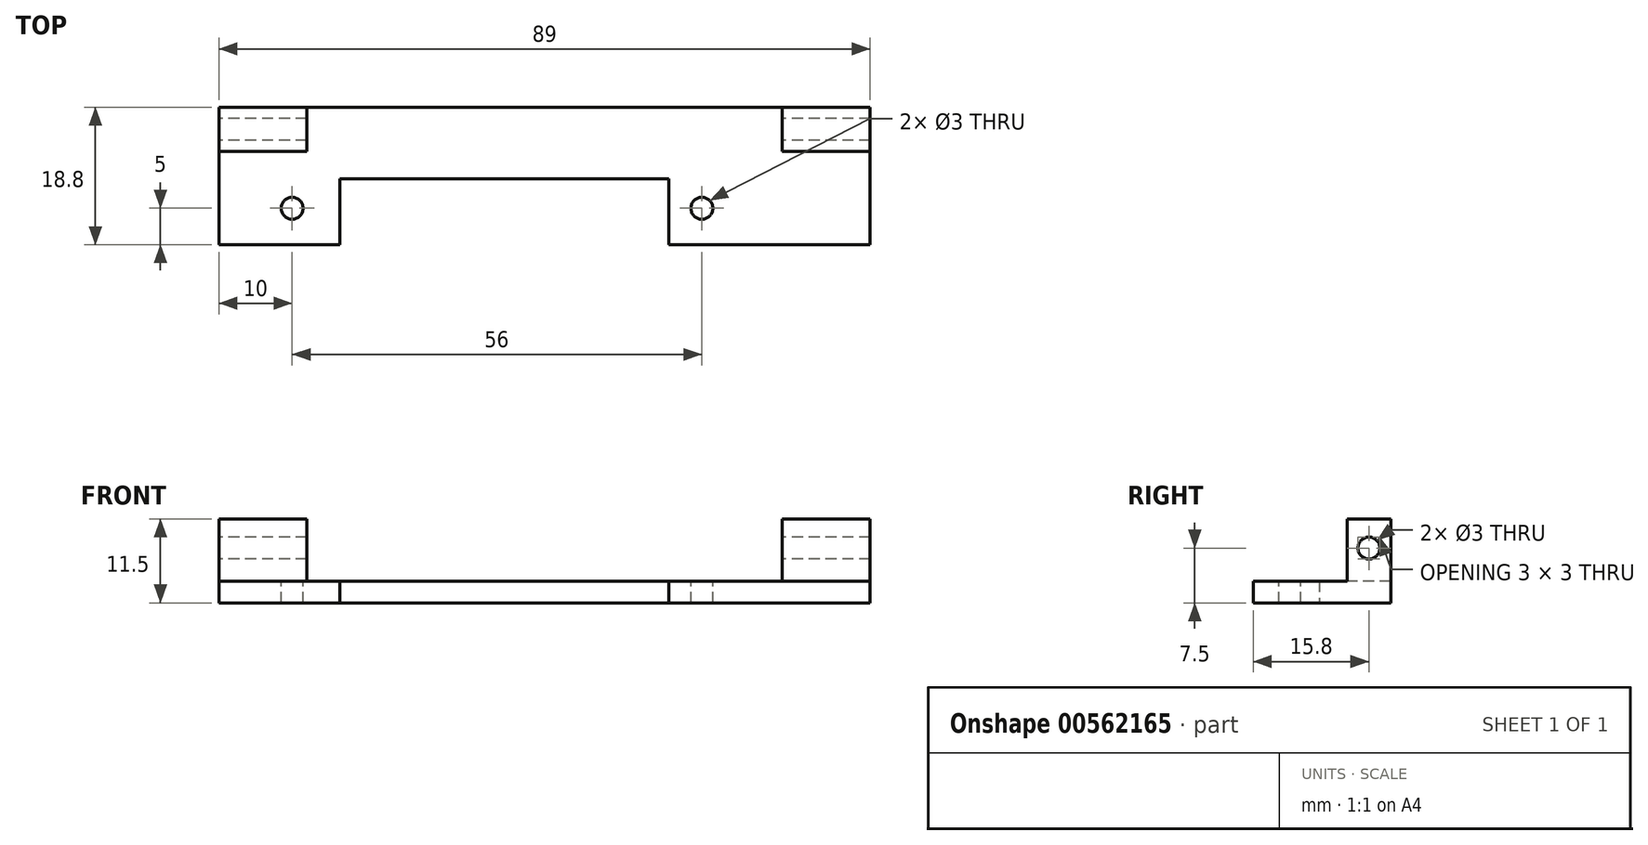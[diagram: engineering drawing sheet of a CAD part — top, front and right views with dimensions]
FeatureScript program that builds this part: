
annotation { "Feature Type Name" : "Feature", "Feature Type Description" : "" }
export const myFeature = defineFeature(function(context is Context, id is Id, definition is map)
    precondition{}
    {
        {
            var Q0;
            Q0=qCreatedBy(makeId("Top.planeOp"),FACE);
            var sketch = newSketch(context, id + "F0", { "sketchPlane" : qUnion([Q0])});
            skLineSegment(sketch, "E0.bottom", {"start": v(44.5, -9.4) * mm, "end": v(-44.5, -9.4) * mm});
            skLineSegment(sketch, "E0.top", {"start": v(44.5, 9.4) * mm, "end": v(-44.5, 9.4) * mm});
            skLineSegment(sketch, "E0.left", {"start": v(44.5, -9.4) * mm, "end": v(44.5, 9.4) * mm});
            skLineSegment(sketch, "E0.right", {"start": v(-44.5, -9.4) * mm, "end": v(-44.5, 9.4) * mm});
            skPoint(sketch, "E0.middle", {"position": v(0, 0) * mm});
            skSolve(sketch);
        }
        {
            var Q0;
            Q0=makeQuery(id+"F0.imprint","IMPRINT",FACE,{"disambiguationData":[TD([[makeQuery(id+"F0.imprint","IMPRINT",EDGE,{"derivedFrom":sQuery(id+"F0.wireOp",EDGE,"E0.bottom")}),-1.0]])]});
            extrude(context, id + "F1", {"entities" : qUnion([Q0]), "depth" : 3 * mm, "offsetDistance" : 25 * mm});
        }
        {
            var Q0;
            Q0=makeQuery(id+"F1.opExtrude","CAP_FACE",FACE,{"disambiguationData":[OSD([sQuery(id+"F0.wireOp",EDGE,"E0.bottom"),sQuery(id+"F0.wireOp",EDGE,"E0.top"),sQuery(id+"F0.wireOp",EDGE,"E0.left"),sQuery(id+"F0.wireOp",EDGE,"E0.right")])],"isStart":false});
            var sketch = newSketch(context, id + "F2", { "sketchPlane" : qUnion([Q0])});
            skLineSegment(sketch, "E1.bottom", {"start": v(44.5, 9.4) * mm, "end": v(32.5, 9.4) * mm});
            skLineSegment(sketch, "E1.top", {"start": v(44.5, 3.4) * mm, "end": v(32.5, 3.4) * mm});
            skLineSegment(sketch, "E1.left", {"start": v(44.5, 9.4) * mm, "end": v(44.5, 3.4) * mm});
            skLineSegment(sketch, "E1.right", {"start": v(32.5, 9.4) * mm, "end": v(32.5, 3.4) * mm});
            skSolve(sketch);
        }
        {
            var Q0;
            {var subQ4=sQuery(id+"F2.wireOp",EDGE,"E1.top");Q0=makeQuery(id+"F2.imprint","IMPRINT",FACE,{"disambiguationData":[TD([[makeQuery(id+"F2.imprint","IMPRINT",EDGE,{"derivedFrom":subQ4}),1.0]])]});}
            var sketch = newSketch(context, id + "F3", { "sketchPlane" : qUnion([Q0])});
            skLineSegment(sketch, "E2.bottom", {"start": v(-44.5, 9.4) * mm, "end": v(-32.5, 9.4) * mm});
            skLineSegment(sketch, "E2.top", {"start": v(-44.5, 3.4) * mm, "end": v(-32.5, 3.4) * mm});
            skLineSegment(sketch, "E2.left", {"start": v(-44.5, 9.4) * mm, "end": v(-44.5, 3.4) * mm});
            skLineSegment(sketch, "E2.right", {"start": v(-32.5, 9.4) * mm, "end": v(-32.5, 3.4) * mm});
            skSolve(sketch);
        }
        {
            var Q0;
            Q0=makeQuery(id+"F2.imprint","IMPRINT",FACE,{"disambiguationData":[TD([[makeQuery(id+"F2.imprint","IMPRINT",EDGE,{"derivedFrom":sQuery(id+"F2.wireOp",EDGE,"E1.bottom")}),1.0]])]});
            var Q1;
            Q1=makeQuery(id+"F3.imprint","IMPRINT",FACE,{"disambiguationData":[TD([[makeQuery(id+"F3.imprint","IMPRINT",EDGE,{"derivedFrom":sQuery(id+"F3.wireOp",EDGE,"E2.bottom")}),1.0]])]});
            extrude(context, id + "F4", {"entities" : qUnion([Q0, Q1]), "operationType" : NewBodyOperationType.ADD, "depth" : 8.5 * mm, "offsetDistance" : 25 * mm});
        }
        {
            var Q0;
            Q0=makeQuery(id+"F4.boolean.opBoolean","MERGE",FACE,{"derivedFrom":[makeQuery(id+"F1.opExtrude","SWEPT_FACE",FACE,{"disambiguationData":[OSD([sQuery(id+"F0.wireOp",EDGE,"E0.right")])]}),makeQuery(id+"F4.opExtrude","SWEPT_FACE",FACE,{"disambiguationData":[OSD([sQuery(id+"F3.wireOp",EDGE,"E2.left")])]})]});
            var sketch = newSketch(context, id + "F5", { "sketchPlane" : qUnion([Q0])});
            skCircle(sketch, "E3", {"center": v(-6.4, 7.5) * mm, "radius": 1.5 * mm});
            skSolve(sketch);
        }
        {
            var Q0;
            Q0=makeQuery(id+"F5.imprint","IMPRINT",FACE,{"disambiguationData":[TD([[makeQuery(id+"F5.imprint","IMPRINT",EDGE,{"derivedFrom":sQuery(id+"F5.wireOp",EDGE,"E3")}),1.0]])]});
            extrude(context, id + "F6", {"entities" : qUnion([Q0]), "operationType" : NewBodyOperationType.REMOVE, "endBound" : BoundingType.THROUGH_ALL, "oppositeDirection" : true, "depth" : 25 * mm, "offsetDistance" : 25 * mm});
        }
        {
            var Q0;
            Q0=makeQuery(id+"F1.opExtrude","CAP_FACE",FACE,{"disambiguationData":[OSD([sQuery(id+"F0.wireOp",EDGE,"E0.bottom"),sQuery(id+"F0.wireOp",EDGE,"E0.top"),sQuery(id+"F0.wireOp",EDGE,"E0.left"),sQuery(id+"F0.wireOp",EDGE,"E0.right")])],"isStart":false});
            var sketch = newSketch(context, id + "F7", { "sketchPlane" : qUnion([Q0])});
            skCircle(sketch, "E4", {"center": v(21.5, -4.4) * mm, "radius": 1.5 * mm});
            skSolve(sketch);
        }
        {
            var Q0;
            Q0=makeQuery(id+"F7.imprint","IMPRINT",FACE,{"disambiguationData":[TD([[makeQuery(id+"F7.imprint","IMPRINT",EDGE,{"derivedFrom":sQuery(id+"F7.wireOp",EDGE,"E4")}),-1.0]])]});
            var sketch = newSketch(context, id + "F8", { "sketchPlane" : qUnion([Q0])});
            skCircle(sketch, "E5", {"center": v(-34.5, -4.4) * mm, "radius": 1.5 * mm});
            skSolve(sketch);
        }
        {
            var Q0;
            Q0=makeQuery(id+"F7.imprint","IMPRINT",FACE,{"disambiguationData":[TD([[makeQuery(id+"F7.imprint","IMPRINT",EDGE,{"derivedFrom":sQuery(id+"F7.wireOp",EDGE,"E4")}),1.0]])]});
            var Q1;
            Q1=makeQuery(id+"F8.imprint","IMPRINT",FACE,{"disambiguationData":[TD([[makeQuery(id+"F8.imprint","IMPRINT",EDGE,{"derivedFrom":sQuery(id+"F8.wireOp",EDGE,"E5")}),1.0]])]});
            extrude(context, id + "F9", {"entities" : qUnion([Q0, Q1]), "operationType" : NewBodyOperationType.REMOVE, "oppositeDirection" : true, "depth" : 15 * mm, "offsetDistance" : 25 * mm});
        }
        {
            var Q0;
            Q0=makeQuery(id+"F1.opExtrude","CAP_FACE",FACE,{"disambiguationData":[OSD([sQuery(id+"F0.wireOp",EDGE,"E0.bottom"),sQuery(id+"F0.wireOp",EDGE,"E0.top"),sQuery(id+"F0.wireOp",EDGE,"E0.left"),sQuery(id+"F0.wireOp",EDGE,"E0.right")])],"isStart":true});
            var sketch = newSketch(context, id + "F10", { "sketchPlane" : qUnion([Q0])});
            skLineSegment(sketch, "E6.bottom", {"start": v(-28, 9.4) * mm, "end": v(17, 9.4) * mm});
            skLineSegment(sketch, "E6.top", {"start": v(-28, 0.4) * mm, "end": v(17, 0.4) * mm});
            skLineSegment(sketch, "E6.left", {"start": v(-28, 9.4) * mm, "end": v(-28, 0.4) * mm});
            skLineSegment(sketch, "E6.right", {"start": v(17, 9.4) * mm, "end": v(17, 0.4) * mm});
            skSolve(sketch);
        }
        {
            var Q0;
            Q0 = qSketchRegion(id + "F10", true);
            extrude(context, id + "F11", {"entities" : qUnion([Q0]), "operationType" : NewBodyOperationType.REMOVE, "oppositeDirection" : true, "depth" : 25 * mm, "offsetDistance" : 25 * mm});
        }
    });
